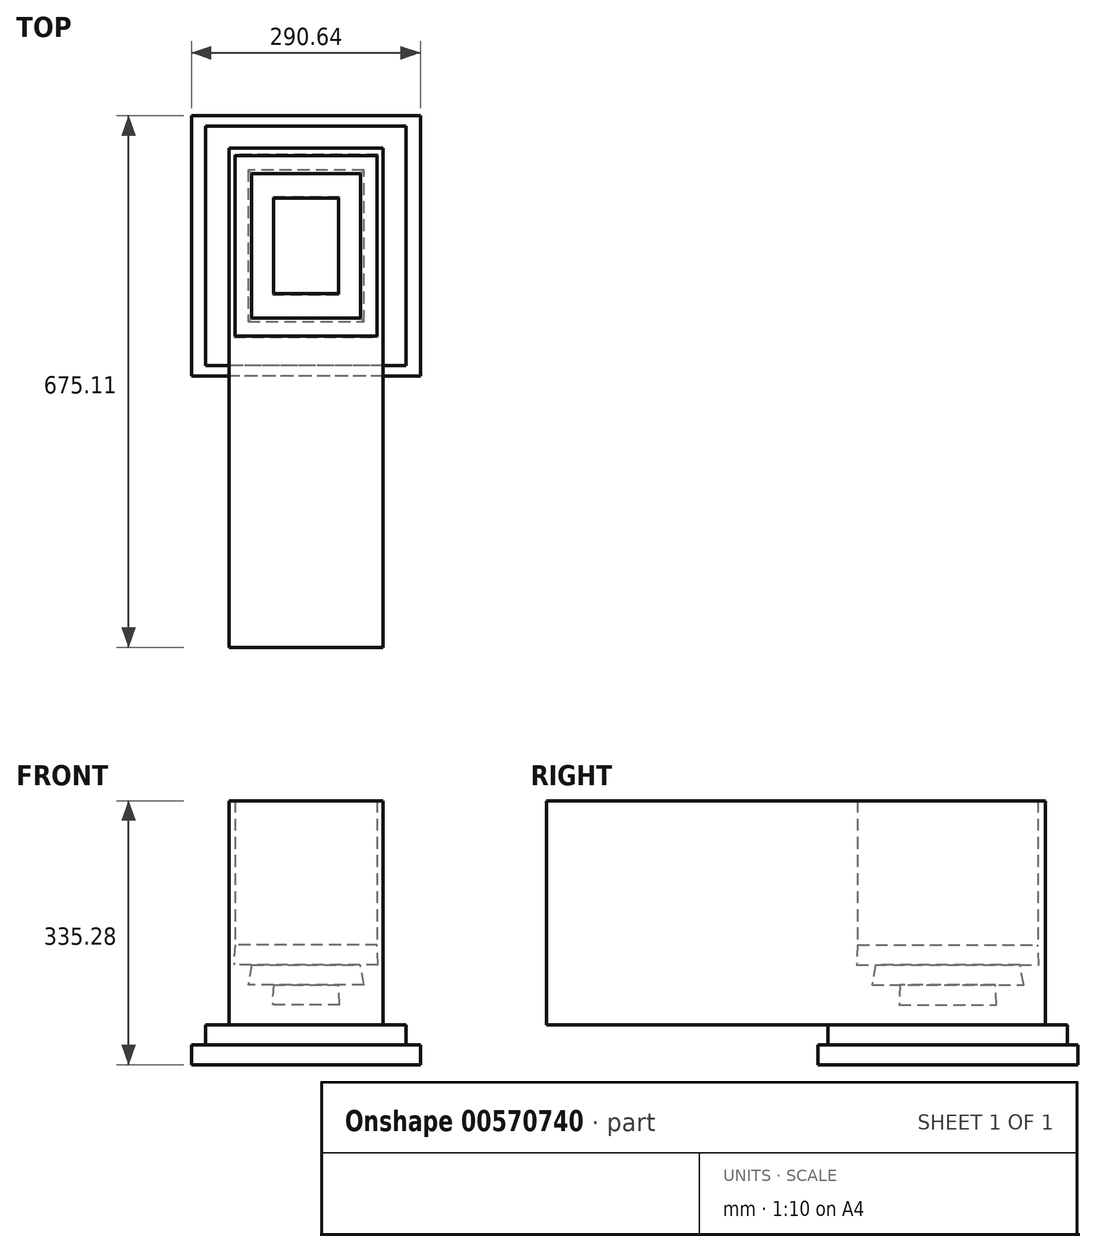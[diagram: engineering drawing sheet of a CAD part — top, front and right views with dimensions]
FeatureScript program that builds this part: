
annotation { "Feature Type Name" : "Feature", "Feature Type Description" : "" }
export const myFeature = defineFeature(function(context is Context, id is Id, definition is map)
    precondition{}
    {
        {
            var Q0;
            Q0=qCreatedBy(makeId("Top.planeOp"),FACE);
            var sketch = newSketch(context, id + "F0", { "sketchPlane" : qUnion([Q0])});
            skLineSegment(sketch, "E0.bottom", {"start": v(145.32, 165.16) * mm, "end": v(-145.32, 165.16) * mm});
            skLineSegment(sketch, "E0.top", {"start": v(145.32, -165.16) * mm, "end": v(-145.32, -165.16) * mm});
            skLineSegment(sketch, "E0.left", {"start": v(145.32, 165.16) * mm, "end": v(145.32, -165.16) * mm});
            skLineSegment(sketch, "E0.right", {"start": v(-145.32, 165.16) * mm, "end": v(-145.32, -165.16) * mm});
            skPoint(sketch, "E0.middle", {"position": v(0, 0) * mm});
            skSolve(sketch);
        }
        {
            var Q0;
            Q0=makeQuery(id+"F0.imprint","IMPRINT",FACE,{"disambiguationData":[TD([[makeQuery(id+"F0.imprint","IMPRINT",EDGE,{"derivedFrom":sQuery(id+"F0.wireOp",EDGE,"E0.bottom")}),1.0]])]});
            extrude(context, id + "F1", {"entities" : qUnion([Q0]), "depth" : 25.4 * mm, "offsetDistance" : 25.4 * mm});
        }
        {
            var Q0;
            Q0=makeQuery(id+"F1.opExtrude","CAP_FACE",FACE,{"disambiguationData":[OSD([sQuery(id+"F0.wireOp",EDGE,"E0.bottom"),sQuery(id+"F0.wireOp",EDGE,"E0.top"),sQuery(id+"F0.wireOp",EDGE,"E0.left"),sQuery(id+"F0.wireOp",EDGE,"E0.right")])],"isStart":false});
            var sketch = newSketch(context, id + "F2", { "sketchPlane" : qUnion([Q0])});
            skLineSegment(sketch, "E1.bottom", {"start": v(127.32, 152.1) * mm, "end": v(-127.32, 152.1) * mm});
            skLineSegment(sketch, "E1.top", {"start": v(127.32, -152.1) * mm, "end": v(-127.32, -152.1) * mm});
            skLineSegment(sketch, "E1.left", {"start": v(127.32, 152.1) * mm, "end": v(127.32, -152.1) * mm});
            skLineSegment(sketch, "E1.right", {"start": v(-127.32, 152.1) * mm, "end": v(-127.32, -152.1) * mm});
            skPoint(sketch, "E1.middle", {"position": v(0, 0) * mm});
            skSolve(sketch);
        }
        {
            var Q0;
            Q0=makeQuery(id+"F2.imprint","IMPRINT",FACE,{"disambiguationData":[TD([[makeQuery(id+"F2.imprint","IMPRINT",EDGE,{"derivedFrom":sQuery(id+"F2.wireOp",EDGE,"E1.bottom")}),1.0]])]});
            extrude(context, id + "F3", {"entities" : qUnion([Q0]), "operationType" : NewBodyOperationType.ADD, "depth" : 25.4 * mm, "offsetDistance" : 25.4 * mm});
        }
        {
            var Q0;
            Q0=makeQuery(id+"F3.opExtrude","CAP_FACE",FACE,{"disambiguationData":[OSD([sQuery(id+"F2.wireOp",EDGE,"E1.bottom"),sQuery(id+"F2.wireOp",EDGE,"E1.top"),sQuery(id+"F2.wireOp",EDGE,"E1.left"),sQuery(id+"F2.wireOp",EDGE,"E1.right")])],"isStart":false});
            var sketch = newSketch(context, id + "F4", { "sketchPlane" : qUnion([Q0])});
            skLineSegment(sketch, "E2.bottom", {"start": v(97.84, 123.87) * mm, "end": v(-97.84, 123.87) * mm});
            skLineSegment(sketch, "E2.top", {"start": v(97.84, -123.87) * mm, "end": v(-97.84, -123.87) * mm});
            skLineSegment(sketch, "E2.left", {"start": v(97.84, 123.87) * mm, "end": v(97.84, -123.87) * mm});
            skLineSegment(sketch, "E2.right", {"start": v(-97.84, 123.87) * mm, "end": v(-97.84, -123.87) * mm});
            skPoint(sketch, "E2.middle", {"position": v(0, 0) * mm});
            skSolve(sketch);
        }
        {
            var Q0;
            Q0=makeQuery(id+"F4.imprint","IMPRINT",FACE,{"disambiguationData":[TD([[makeQuery(id+"F4.imprint","IMPRINT",EDGE,{"derivedFrom":sQuery(id+"F4.wireOp",EDGE,"E2.bottom")}),1.0]])]});
            extrude(context, id + "F5", {"entities" : qUnion([Q0]), "operationType" : NewBodyOperationType.ADD, "depth" : 101.6 * mm, "offsetDistance" : 25.4 * mm});
        }
        {
            var Q0;
            Q0=makeQuery(id+"F5.opExtrude","CAP_FACE",FACE,{"disambiguationData":[OSD([sQuery(id+"F4.wireOp",EDGE,"E2.bottom"),sQuery(id+"F4.wireOp",EDGE,"E2.top"),sQuery(id+"F4.wireOp",EDGE,"E2.left"),sQuery(id+"F4.wireOp",EDGE,"E2.right")])],"isStart":false});
            var sketch = newSketch(context, id + "F6", { "sketchPlane" : qUnion([Q0])});
            skLineSegment(sketch, "E3.bottom", {"start": v(90.32, 114.46) * mm, "end": v(-90.32, 114.46) * mm});
            skLineSegment(sketch, "E3.top", {"start": v(90.32, -114.46) * mm, "end": v(-90.32, -114.46) * mm});
            skLineSegment(sketch, "E3.left", {"start": v(90.32, 114.46) * mm, "end": v(90.32, -114.46) * mm});
            skLineSegment(sketch, "E3.right", {"start": v(-90.32, 114.46) * mm, "end": v(-90.32, -114.46) * mm});
            skPoint(sketch, "E3.middle", {"position": v(0, 0) * mm});
            skSolve(sketch);
        }
        {
            var Q0;
            Q0=makeQuery(id+"F6.imprint","IMPRINT",FACE,{"disambiguationData":[TD([[makeQuery(id+"F6.imprint","IMPRINT",EDGE,{"derivedFrom":sQuery(id+"F6.wireOp",EDGE,"E3.bottom")}),1.0]])]});
            extrude(context, id + "F7", {"entities" : qUnion([Q0]), "operationType" : NewBodyOperationType.REMOVE, "oppositeDirection" : true, "depth" : 25.4 * mm, "offsetDistance" : 25.4 * mm, "hasDraft" : true, "draftAngle" : 3 * degree});
        }
        {
            var Q0;
            Q0=makeQuery(id+"F7.boolean.opBoolean","COPY",FACE,{"derivedFrom":makeQuery(id+"F7.opExtrude","CAP_FACE",FACE,{"disambiguationData":[OSD([sQuery(id+"F6.wireOp",EDGE,"E3.bottom"),sQuery(id+"F6.wireOp",EDGE,"E3.top"),sQuery(id+"F6.wireOp",EDGE,"E3.left"),sQuery(id+"F6.wireOp",EDGE,"E3.right")])],"isStart":false})});
            var sketch = newSketch(context, id + "F8", { "sketchPlane" : qUnion([Q0])});
            skLineSegment(sketch, "E4.bottom", {"start": v(69, 91.88) * mm, "end": v(-69, 91.88) * mm});
            skLineSegment(sketch, "E4.top", {"start": v(69, -91.88) * mm, "end": v(-69, -91.88) * mm});
            skLineSegment(sketch, "E4.left", {"start": v(69, 91.88) * mm, "end": v(69, -91.88) * mm});
            skLineSegment(sketch, "E4.right", {"start": v(-69, 91.88) * mm, "end": v(-69, -91.88) * mm});
            skPoint(sketch, "E4.middle", {"position": v(0, 0) * mm});
            skSolve(sketch);
        }
        {
            var Q0;
            Q0=makeQuery(id+"F8.imprint","IMPRINT",FACE,{"disambiguationData":[TD([[makeQuery(id+"F8.imprint","IMPRINT",EDGE,{"derivedFrom":sQuery(id+"F8.wireOp",EDGE,"E4.bottom")}),1.0]])]});
            extrude(context, id + "F9", {"entities" : qUnion([Q0]), "operationType" : NewBodyOperationType.REMOVE, "oppositeDirection" : true, "depth" : 25.4 * mm, "offsetDistance" : 25.4 * mm, "hasDraft" : true, "draftAngle" : 10 * degree});
        }
        {
            var Q0;
            Q0=makeQuery(id+"F9.boolean.opBoolean","COPY",FACE,{"derivedFrom":makeQuery(id+"F9.opExtrude","CAP_FACE",FACE,{"disambiguationData":[OSD([sQuery(id+"F8.wireOp",EDGE,"E4.bottom"),sQuery(id+"F8.wireOp",EDGE,"E4.top"),sQuery(id+"F8.wireOp",EDGE,"E4.left"),sQuery(id+"F8.wireOp",EDGE,"E4.right")])],"isStart":false})});
            var sketch = newSketch(context, id + "F10", { "sketchPlane" : qUnion([Q0])});
            skLineSegment(sketch, "E5.bottom", {"start": v(41.4, 60.52) * mm, "end": v(-41.4, 60.52) * mm});
            skLineSegment(sketch, "E5.top", {"start": v(41.4, -60.52) * mm, "end": v(-41.4, -60.52) * mm});
            skLineSegment(sketch, "E5.left", {"start": v(41.4, 60.52) * mm, "end": v(41.4, -60.52) * mm});
            skLineSegment(sketch, "E5.right", {"start": v(-41.4, 60.52) * mm, "end": v(-41.4, -60.52) * mm});
            skPoint(sketch, "E5.middle", {"position": v(0, 0) * mm});
            skSolve(sketch);
        }
        {
            var Q0;
            Q0=makeQuery(id+"F10.imprint","IMPRINT",FACE,{"disambiguationData":[TD([[makeQuery(id+"F10.imprint","IMPRINT",EDGE,{"derivedFrom":sQuery(id+"F10.wireOp",EDGE,"E5.bottom")}),1.0]])]});
            extrude(context, id + "F11", {"entities" : qUnion([Q0]), "operationType" : NewBodyOperationType.REMOVE, "oppositeDirection" : true, "depth" : 25.4 * mm, "offsetDistance" : 25.4 * mm, "hasDraft" : true, "draftAngle" : 3 * degree});
        }
        {
            var Q0;
            Q0=makeQuery(id+"F5.opExtrude","SWEPT_FACE",FACE,{"disambiguationData":[OSD([sQuery(id+"F4.wireOp",EDGE,"E2.top")])]});
            extrude(context, id + "F12", {"entities" : qUnion([Q0]), "operationType" : NewBodyOperationType.ADD, "depth" : 132.08 * mm, "offsetDistance" : 25.4 * mm});
        }
        {
            var Q0;
            {var subQ0=sQuery(id+"F4.wireOp",EDGE,"E2.top");Q0=makeQuery(id+"F12.boolean.opBoolean","MERGE",FACE,{"derivedFrom":[makeQuery(id+"F5.opExtrude","CAP_FACE",FACE,{"disambiguationData":[OSD([sQuery(id+"F4.wireOp",EDGE,"E2.bottom"),subQ0,sQuery(id+"F4.wireOp",EDGE,"E2.left"),sQuery(id+"F4.wireOp",EDGE,"E2.right")])],"isStart":false}),makeQuery(id+"F12.opExtrude","SWEPT_FACE",FACE,{"disambiguationData":[OSD([subQ0]),TDD([makeQuery(id+"F5.opExtrude","CAP_EDGE",EDGE,{"disambiguationData":[OSD([subQ0])],"isStart":false})])]})]});}
            extrude(context, id + "F13", {"entities" : qUnion([Q0]), "operationType" : NewBodyOperationType.ADD, "depth" : 99.06 * mm, "offsetDistance" : 25.4 * mm});
        }
        {
            var Q0;
            Q0=makeQuery(id+"F13.opExtrude","CAP_FACE",FACE,{"disambiguationData":[OSD([sQuery(id+"F4.wireOp",EDGE,"E2.bottom"),sQuery(id+"F4.wireOp",EDGE,"E2.top"),sQuery(id+"F4.wireOp",EDGE,"E2.left"),sQuery(id+"F4.wireOp",EDGE,"E2.right")])],"isStart":false});
            extrude(context, id + "F14", {"entities" : qUnion([Q0]), "operationType" : NewBodyOperationType.ADD, "depth" : 83.82 * mm, "offsetDistance" : 25.4 * mm});
        }
        {
            var Q0;
            {var subQ0=sQuery(id+"F4.wireOp",EDGE,"E2.top");Q0=makeQuery(id+"F14.boolean.opBoolean","MERGE",FACE,{"derivedFrom":[makeQuery(id+"F13.boolean.opBoolean","MERGE",FACE,{"derivedFrom":[makeQuery(id+"F12.opExtrude","CAP_FACE",FACE,{"disambiguationData":[OSD([subQ0])],"isStart":false}),makeQuery(id+"F13.opExtrude","SWEPT_FACE",FACE,{"disambiguationData":[OSD([subQ0])]})]}),makeQuery(id+"F14.opExtrude","SWEPT_FACE",FACE,{"disambiguationData":[OSD([subQ0])]})]});}
            extrude(context, id + "F15", {"entities" : qUnion([Q0]), "operationType" : NewBodyOperationType.ADD, "depth" : 254 * mm, "offsetDistance" : 25.4 * mm});
        }
    });
